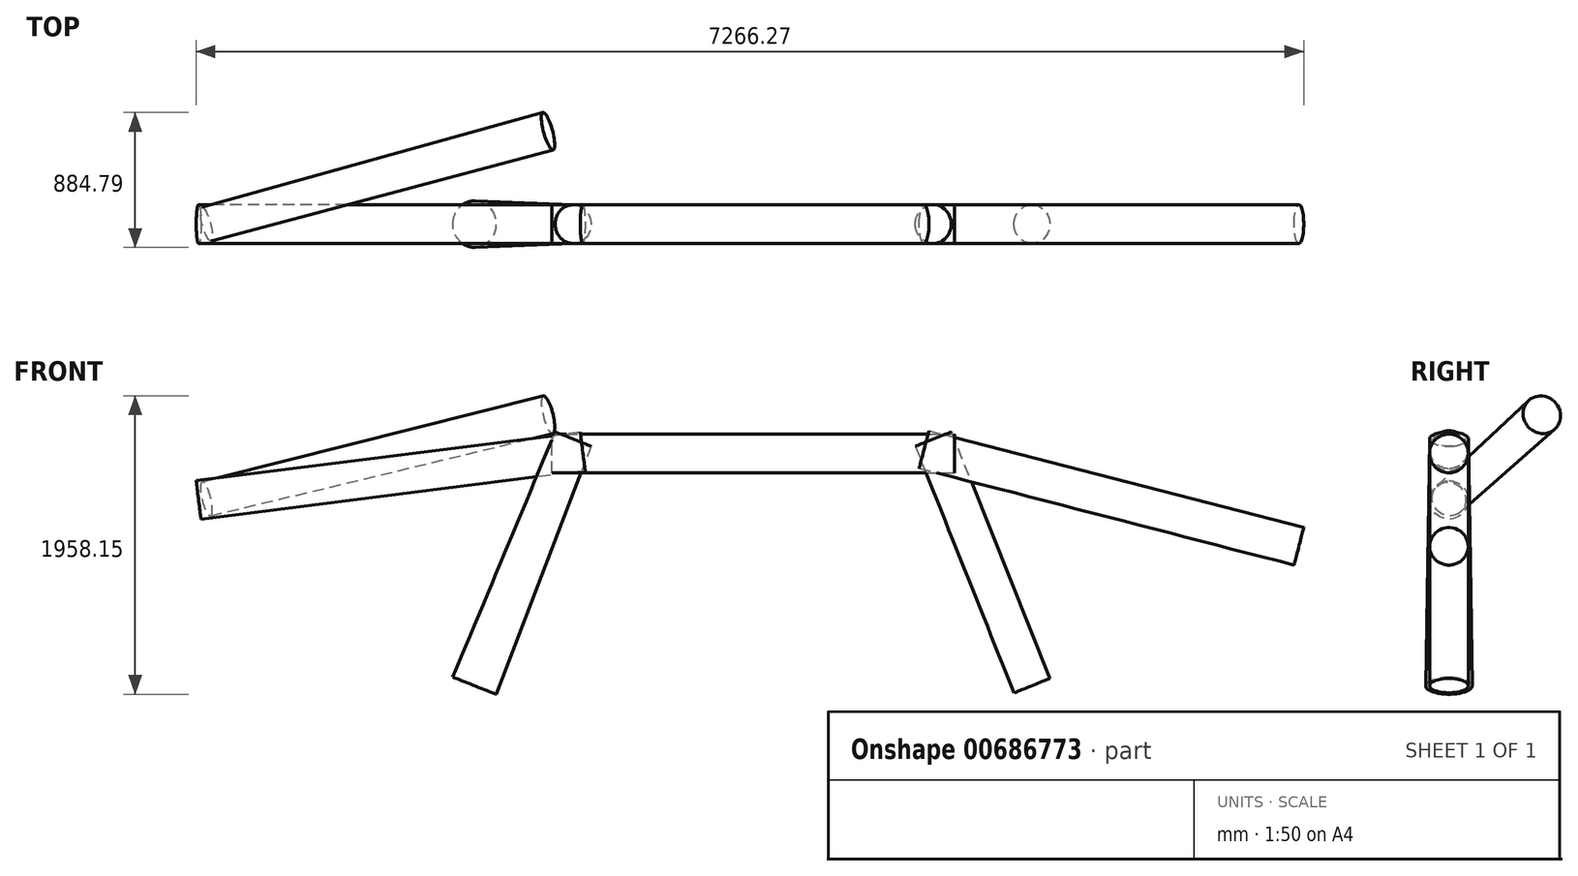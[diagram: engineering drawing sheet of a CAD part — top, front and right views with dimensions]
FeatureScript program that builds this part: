
annotation { "Feature Type Name" : "Feature", "Feature Type Description" : "" }
export const myFeature = defineFeature(function(context is Context, id is Id, definition is map)
    precondition{}
    {
        {
            var Q0;
            Q0=qCreatedBy(makeId("Front.planeOp"),FACE);
            var sketch = newSketch(context, id + "F0", { "sketchPlane" : qUnion([Q0])});
            skLineSegment(sketch, "E0", {"start": v(-1320.8, 0) * mm, "end": v(-1219.2, 0) * mm, "construction": true});
            skLineSegment(sketch, "E1", {"start": v(-1219.2, 0) * mm, "end": v(1219.2, 0) * mm, "construction": true});
            skLineSegment(sketch, "E2", {"start": v(1219.2, 0) * mm, "end": v(1320.8, 0) * mm, "construction": true});
            skLineSegment(sketch, "E3", {"start": v(-1181.47, 94.33) * mm, "end": v(-1219.2, 0) * mm, "construction": true});
            skLineSegment(sketch, "E4", {"start": v(-1219.2, 0) * mm, "end": v(-1828.8, -1524) * mm, "construction": true});
            skLineSegment(sketch, "E5", {"start": v(1181.47, 94.33) * mm, "end": v(1219.2, 0) * mm, "construction": true});
            skLineSegment(sketch, "E6", {"start": v(1219.2, 0) * mm, "end": v(1828.8, -1524) * mm, "construction": true});
            skLineSegment(sketch, "E7", {"start": v(1120.83, 25.4) * mm, "end": v(1219.2, 0) * mm, "construction": true});
            skLineSegment(sketch, "E8", {"start": v(1219.2, 0) * mm, "end": v(3580.17, -609.6) * mm, "construction": true});
            skLineSegment(sketch, "E9", {"start": v(-1118.4, 12.7) * mm, "end": v(-1219.2, 0) * mm, "construction": true});
            skLineSegment(sketch, "E10", {"start": v(-1219.2, 0) * mm, "end": v(-3638.47, -304.8) * mm, "construction": true});
            skPoint(sketch, "E11", {"position": v(-3587.67, -298.4) * mm});
            skSolve(sketch);
        }
        {
            var Q0;
            Q0=qCreatedBy(makeId("Top.planeOp"),FACE);
            var sketch = newSketch(context, id + "F1", { "sketchPlane" : qUnion([Q0])});
            skLineSegment(sketch, "E12", {"start": v(0, 0) * mm, "end": v(0, 609.6) * mm, "construction": true});
            skLineSegment(sketch, "E13", {"start": v(0, 0) * mm, "end": v(0, -609.6) * mm, "construction": true});
            skSolve(sketch);
        }
        {
            var Q0;
            Q0=sQuery(id+"F1.wireOp",EDGE,"E12");
            var Q1;
            Q1=sQuery(id+"F1.wireOp",VERTEX,"E12.end");
            cPlane(context, id + "F2", {"entities" : qUnion([Q0, Q1]), "cplaneType" : CPlaneType.LINE_POINT, "offset" : 25.4 * mm, "width" : 152.4 * mm, "height" : 152.4 * mm});
        }
        {
            var Q0;
            Q0=sQuery(id+"F0.wireOp",EDGE,"E10");
            var Q1;
            Q1=sQuery(id+"F0.wireOp",VERTEX,"E10.end");
            cPlane(context, id + "F3", {"entities" : qUnion([Q0, Q1]), "cplaneType" : CPlaneType.LINE_POINT, "offset" : 25.4 * mm, "width" : 152.4 * mm, "height" : 152.4 * mm});
        }
        {
            var Q0;
            Q0=sQuery(id+"F0.wireOp",VERTEX,"E9.start");
            var Q1;
            Q1=sQuery(id+"F0.wireOp",EDGE,"E9");
            cPlane(context, id + "F4", {"entities" : qUnion([Q0, Q1]), "cplaneType" : CPlaneType.LINE_POINT, "offset" : 25.4 * mm, "width" : 152.4 * mm, "height" : 152.4 * mm});
        }
        {
            var Q0;
            Q0=qCreatedBy(id+"F3.planeOp",FACE);
            var sketch = newSketch(context, id + "F5", { "sketchPlane" : qUnion([Q0])});
            skCircle(sketch, "E14", {"center": v(0, 152.4) * mm, "radius": 127 * mm});
            skSolve(sketch);
        }
        {
            var Q0;
            Q0=qCreatedBy(id+"F4.planeOp",FACE);
            var sketch = newSketch(context, id + "F6", { "sketchPlane" : qUnion([Q0])});
            skCircle(sketch, "E15", {"center": v(0, 152.4) * mm, "radius": 127 * mm});
            skSolve(sketch);
        }
        {
            var Q0;
            Q0=makeQuery(id+"F5.imprint","IMPRINT",FACE,{"disambiguationData":[TD([[makeQuery(id+"F5.imprint","IMPRINT",EDGE,{"derivedFrom":sQuery(id+"F5.wireOp",EDGE,"E14")}),1.0]])]});
            var Q1;
            Q1=makeQuery(id+"F6.imprint","IMPRINT",FACE,{"disambiguationData":[TD([[makeQuery(id+"F6.imprint","IMPRINT",EDGE,{"derivedFrom":sQuery(id+"F6.wireOp",EDGE,"E15")}),1.0]])]});
            loft(context, id + "F7", {"sheetProfilesArray" : [{ "sheetProfileEntities" : qUnion([Q0]) }, { "sheetProfileEntities" : qUnion([Q1]) }]});
        }
        {
            var Q0;
            Q0=sQuery(id+"F0.wireOp",EDGE,"E4");
            var Q1;
            Q1=sQuery(id+"F0.wireOp",VERTEX,"E4.end");
            cPlane(context, id + "F8", {"entities" : qUnion([Q0, Q1]), "cplaneType" : CPlaneType.LINE_POINT, "offset" : 25.4 * mm, "width" : 152.4 * mm, "height" : 152.4 * mm});
        }
        {
            var Q0;
            Q0=sQuery(id+"F0.wireOp",VERTEX,"E3.start");
            var Q1;
            Q1=sQuery(id+"F0.wireOp",EDGE,"E3");
            cPlane(context, id + "F9", {"entities" : qUnion([Q0, Q1]), "cplaneType" : CPlaneType.LINE_POINT, "offset" : 25.4 * mm, "width" : 152.4 * mm, "height" : 152.4 * mm});
        }
        {
            var Q0;
            Q0=qCreatedBy(id+"F8.planeOp",FACE);
            var sketch = newSketch(context, id + "F10", { "sketchPlane" : qUnion([Q0])});
            skCircle(sketch, "E16", {"center": v(-1132, 0) * mm, "radius": 152.4 * mm});
            skSolve(sketch);
        }
        {
            var Q0;
            Q0=qCreatedBy(id+"F9.planeOp",FACE);
            var sketch = newSketch(context, id + "F11", { "sketchPlane" : qUnion([Q0])});
            skCircle(sketch, "E17", {"center": v(-1132, 0) * mm, "radius": 127 * mm});
            skSolve(sketch);
        }
        {
            var Q0;
            Q0=makeQuery(id+"F10.imprint","IMPRINT",FACE,{"disambiguationData":[TD([[makeQuery(id+"F10.imprint","IMPRINT",EDGE,{"derivedFrom":sQuery(id+"F10.wireOp",EDGE,"E16")}),1.0]])]});
            var Q1;
            Q1=makeQuery(id+"F11.imprint","IMPRINT",FACE,{"disambiguationData":[TD([[makeQuery(id+"F11.imprint","IMPRINT",EDGE,{"derivedFrom":sQuery(id+"F11.wireOp",EDGE,"E17")}),1.0]])]});
            loft(context, id + "F12", {"sheetProfilesArray" : [{ "sheetProfileEntities" : qUnion([Q0]) }, { "sheetProfileEntities" : qUnion([Q1]) }]});
        }
        {
            var Q0;
            Q0=sQuery(id+"F0.wireOp",EDGE,"E0");
            var Q1;
            Q1=sQuery(id+"F0.wireOp",VERTEX,"E0.start");
            cPlane(context, id + "F13", {"entities" : qUnion([Q0, Q1]), "cplaneType" : CPlaneType.LINE_POINT, "offset" : 25.4 * mm, "width" : 152.4 * mm, "height" : 152.4 * mm});
        }
        {
            var Q0;
            Q0=sQuery(id+"F0.wireOp",EDGE,"E2");
            var Q1;
            Q1=sQuery(id+"F0.wireOp",VERTEX,"E2.end");
            cPlane(context, id + "F14", {"entities" : qUnion([Q0, Q1]), "cplaneType" : CPlaneType.LINE_POINT, "offset" : 25.4 * mm, "width" : 152.4 * mm, "height" : 152.4 * mm});
        }
        {
            var Q0;
            Q0=qCreatedBy(id+"F14.planeOp",FACE);
            var sketch = newSketch(context, id + "F15", { "sketchPlane" : qUnion([Q0])});
            skCircle(sketch, "E18", {"center": v(0, 0) * mm, "radius": 127 * mm});
            skSolve(sketch);
        }
        {
            var Q0;
            Q0=qCreatedBy(id+"F13.planeOp",FACE);
            var sketch = newSketch(context, id + "F16", { "sketchPlane" : qUnion([Q0])});
            skCircle(sketch, "E19", {"center": v(0, 0) * mm, "radius": 127 * mm});
            skSolve(sketch);
        }
        {
            var Q0;
            Q0=makeQuery(id+"F16.imprint","IMPRINT",FACE,{"disambiguationData":[TD([[makeQuery(id+"F16.imprint","IMPRINT",EDGE,{"derivedFrom":sQuery(id+"F16.wireOp",EDGE,"E19")}),1.0]])]});
            var Q1;
            Q1=makeQuery(id+"F15.imprint","IMPRINT",FACE,{"disambiguationData":[TD([[makeQuery(id+"F15.imprint","IMPRINT",EDGE,{"derivedFrom":sQuery(id+"F15.wireOp",EDGE,"E18")}),1.0]])]});
            loft(context, id + "F17", {"sheetProfilesArray" : [{ "sheetProfileEntities" : qUnion([Q0]) }, { "sheetProfileEntities" : qUnion([Q1]) }]});
        }
        {
            var Q0;
            Q0=sQuery(id+"F0.wireOp",VERTEX,"E8.end");
            var Q1;
            Q1=sQuery(id+"F0.wireOp",EDGE,"E8");
            cPlane(context, id + "F18", {"entities" : qUnion([Q0, Q1]), "cplaneType" : CPlaneType.LINE_POINT, "offset" : 25.4 * mm, "width" : 152.4 * mm, "height" : 152.4 * mm});
        }
        {
            var Q0;
            Q0=sQuery(id+"F0.wireOp",EDGE,"E7");
            var Q1;
            Q1=sQuery(id+"F0.wireOp",VERTEX,"E7.start");
            cPlane(context, id + "F19", {"entities" : qUnion([Q0, Q1]), "cplaneType" : CPlaneType.LINE_POINT, "offset" : 25.4 * mm, "width" : 152.4 * mm, "height" : 152.4 * mm});
        }
        {
            var Q0;
            Q0=qCreatedBy(id+"F18.planeOp",FACE);
            var sketch = newSketch(context, id + "F20", { "sketchPlane" : qUnion([Q0])});
            skCircle(sketch, "E20", {"center": v(0, 304.8) * mm, "radius": 127 * mm});
            skSolve(sketch);
        }
        {
            var Q0;
            Q0=qCreatedBy(id+"F19.planeOp",FACE);
            var sketch = newSketch(context, id + "F21", { "sketchPlane" : qUnion([Q0])});
            skCircle(sketch, "E21", {"center": v(0, 304.8) * mm, "radius": 127 * mm});
            skSolve(sketch);
        }
        {
            var Q0;
            Q0=makeQuery(id+"F20.imprint","IMPRINT",FACE,{"disambiguationData":[TD([[makeQuery(id+"F20.imprint","IMPRINT",EDGE,{"derivedFrom":sQuery(id+"F20.wireOp",EDGE,"E20")}),1.0]])]});
            var Q1;
            Q1=makeQuery(id+"F21.imprint","IMPRINT",FACE,{"disambiguationData":[TD([[makeQuery(id+"F21.imprint","IMPRINT",EDGE,{"derivedFrom":sQuery(id+"F21.wireOp",EDGE,"E21")}),1.0]])]});
            loft(context, id + "F22", {"sheetProfilesArray" : [{ "sheetProfileEntities" : qUnion([Q0]) }, { "sheetProfileEntities" : qUnion([Q1]) }]});
        }
        {
            var Q0;
            Q0=sQuery(id+"F0.wireOp",EDGE,"E6");
            var Q1;
            Q1=sQuery(id+"F0.wireOp",VERTEX,"E6.end");
            cPlane(context, id + "F23", {"entities" : qUnion([Q0, Q1]), "cplaneType" : CPlaneType.LINE_POINT, "offset" : 25.4 * mm, "width" : 152.4 * mm, "height" : 152.4 * mm});
        }
        {
            var Q0;
            Q0=sQuery(id+"F0.wireOp",EDGE,"E5");
            var Q1;
            Q1=sQuery(id+"F0.wireOp",VERTEX,"E5.start");
            cPlane(context, id + "F24", {"entities" : qUnion([Q0, Q1]), "cplaneType" : CPlaneType.LINE_POINT, "offset" : 25.4 * mm, "width" : 152.4 * mm, "height" : 152.4 * mm});
        }
        {
            var Q0;
            Q0=qCreatedBy(id+"F24.planeOp",FACE);
            var sketch = newSketch(context, id + "F25", { "sketchPlane" : qUnion([Q0])});
            skCircle(sketch, "E22", {"center": v(1132, 0) * mm, "radius": 127 * mm});
            skSolve(sketch);
        }
        {
            var Q0;
            Q0=qCreatedBy(id+"F23.planeOp",FACE);
            var sketch = newSketch(context, id + "F26", { "sketchPlane" : qUnion([Q0])});
            skCircle(sketch, "E23", {"center": v(1132, 0) * mm, "radius": 127 * mm});
            skSolve(sketch);
        }
        {
            var Q0;
            Q0=makeQuery(id+"F26.imprint","IMPRINT",FACE,{"disambiguationData":[TD([[makeQuery(id+"F26.imprint","IMPRINT",EDGE,{"derivedFrom":sQuery(id+"F26.wireOp",EDGE,"E23")}),1.0]])]});
            var Q1;
            Q1=makeQuery(id+"F25.imprint","IMPRINT",FACE,{"disambiguationData":[TD([[makeQuery(id+"F25.imprint","IMPRINT",EDGE,{"derivedFrom":sQuery(id+"F25.wireOp",EDGE,"E22")}),1.0]])]});
            loft(context, id + "F27", {"sheetProfilesArray" : [{ "sheetProfileEntities" : qUnion([Q0]) }, { "sheetProfileEntities" : qUnion([Q1]) }]});
        }
        {
            var Q0;
            Q0=qCreatedBy(id+"F2.planeOp",FACE);
            var sketch = newSketch(context, id + "F28", { "sketchPlane" : qUnion([Q0])});
            skLineSegment(sketch, "E24", {"start": v(-1320.8, 0) * mm, "end": v(-1219.2, 0) * mm, "construction": true});
            skLineSegment(sketch, "E25", {"start": v(-1219.2, 0) * mm, "end": v(1219.2, 0) * mm, "construction": true});
            skLineSegment(sketch, "E26", {"start": v(1219.2, 0) * mm, "end": v(1320.8, 0) * mm, "construction": true});
            skLineSegment(sketch, "E27", {"start": v(-1181.47, 94.33) * mm, "end": v(-1219.2, 0) * mm, "construction": true});
            skLineSegment(sketch, "E28", {"start": v(-1219.2, 0) * mm, "end": v(-1828.8, -1524) * mm, "construction": true});
            skLineSegment(sketch, "E29", {"start": v(1181.47, 94.33) * mm, "end": v(1219.2, 0) * mm, "construction": true});
            skLineSegment(sketch, "E30", {"start": v(1219.2, 0) * mm, "end": v(1828.8, -1524) * mm, "construction": true});
            skLineSegment(sketch, "E31", {"start": v(1118.4, 12.7) * mm, "end": v(1219.2, 0) * mm, "construction": true});
            skLineSegment(sketch, "E32", {"start": v(1219.2, 0) * mm, "end": v(3638.47, -304.8) * mm, "construction": true});
            skLineSegment(sketch, "E33", {"start": v(-1120.83, 25.4) * mm, "end": v(-1219.2, 0) * mm, "construction": true});
            skLineSegment(sketch, "E34", {"start": v(-1219.2, 0) * mm, "end": v(-3580.17, -609.6) * mm, "construction": true});
            skLineSegment(sketch, "E35", {"start": v(1117.6, 254) * mm, "end": v(-1117.6, 127) * mm, "construction": true});
            skPoint(sketch, "E36", {"position": v(1346.2, 254) * mm});
            skSolve(sketch);
        }
        {
            var Q0;
            Q0=sQuery(id+"F28.wireOp",VERTEX,"E36");
            var Q1;
            Q1=sQuery(id+"F0.wireOp",VERTEX,"E10.end");
            var Q2;
            Q2=sQuery(id+"F0.wireOp",VERTEX,"E4.start");
            cPlane(context, id + "F29", {"entities" : qUnion([Q0, Q1, Q2]), "cplaneType" : CPlaneType.THREE_POINT, "offset" : 25.4 * mm, "width" : 152.4 * mm, "height" : 152.4 * mm});
        }
        {
            var Q0;
            Q0=qCreatedBy(id+"F29.planeOp",FACE);
            var sketch = newSketch(context, id + "F30", { "sketchPlane" : qUnion([Q0])});
            skLineSegment(sketch, "E37", {"start": v(-1339.03, -660.24) * mm, "end": v(-3595.33, 120.84) * mm, "construction": true});
            skSolve(sketch);
        }
        {
            var Q0;
            Q0=sQuery(id+"F30.wireOp",EDGE,"E37");
            var Q1;
            Q1=sQuery(id+"F28.wireOp",VERTEX,"E36");
            cPlane(context, id + "F31", {"entities" : qUnion([Q0, Q1]), "cplaneType" : CPlaneType.LINE_POINT, "offset" : 25.4 * mm, "width" : 152.4 * mm, "height" : 152.4 * mm});
        }
        {
            var Q0;
            Q0=sQuery(id+"F30.wireOp",EDGE,"E37");
            var Q1;
            Q1=sQuery(id+"F0.wireOp",VERTEX,"E11");
            cPlane(context, id + "F32", {"entities" : qUnion([Q0, Q1]), "cplaneType" : CPlaneType.LINE_POINT, "offset" : 25.4 * mm, "width" : 152.4 * mm, "height" : 152.4 * mm});
        }
        {
            var Q0;
            Q0=qCreatedBy(id+"F31.planeOp",FACE);
            var sketch = newSketch(context, id + "F33", { "sketchPlane" : qUnion([Q0])});
            skCircle(sketch, "E38", {"center": v(-907.6, 568.75) * mm, "radius": 127 * mm});
            skSolve(sketch);
        }
        {
            var Q0;
            Q0=qCreatedBy(id+"F32.planeOp",FACE);
            var sketch = newSketch(context, id + "F34", { "sketchPlane" : qUnion([Q0])});
            skCircle(sketch, "E39", {"center": v(-907.6, 568.75) * mm, "radius": 114.3 * mm});
            skSolve(sketch);
        }
        {
            var Q1;
            Q1 = qSketchRegion(id + "F34", true);
            var Q2;
            Q2 = qSketchRegion(id + "F33", true);
            loft(context, id + "F35", {"sheetProfilesArray" : [{ "sheetProfileEntities" : qUnion([Q1]) }, { "sheetProfileEntities" : qUnion([Q2]) }]});
        }
    });
